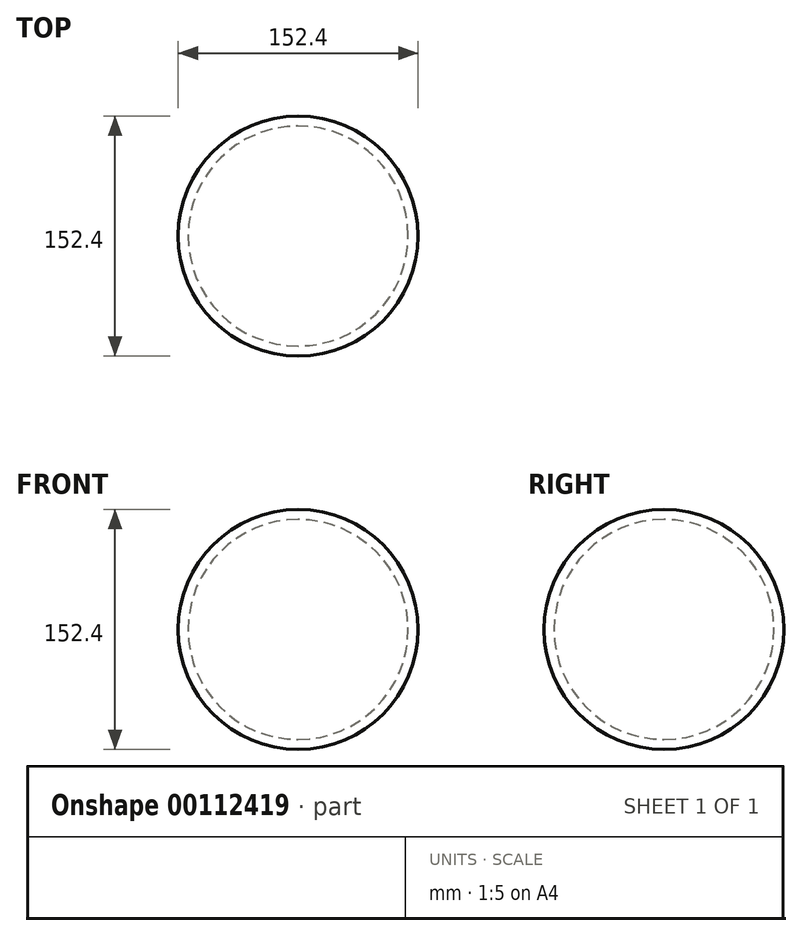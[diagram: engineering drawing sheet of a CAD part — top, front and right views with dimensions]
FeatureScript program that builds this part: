
annotation { "Feature Type Name" : "Feature", "Feature Type Description" : "" }
export const myFeature = defineFeature(function(context is Context, id is Id, definition is map)
    precondition{}
    {
        {
            var Q0;
            Q0=qCreatedBy(makeId("Front.planeOp"),FACE);
            var sketch = newSketch(context, id + "F0", { "sketchPlane" : qUnion([Q0])});
            skCircle(sketch, "E0", {"center": v(0, 0) * mm, "radius": 76.2 * mm});
            skCircle(sketch, "E1", {"center": v(0, 0) * mm, "radius": 69.89 * mm});
            skLineSegment(sketch, "E2", {"start": v(0, 76.2) * mm, "end": v(0, -76.2) * mm});
            skSolve(sketch);
        }
        {
            var Q0;
            {var subQ0=sQuery(id+"F0.wireOp",EDGE,"E2");var subQ1=sQuery(id+"F0.wireOp",EDGE,"E0");var subQ2=makeQuery(id+"F0.imprint","INTERSECT",VERTEX,{"disambiguationData":[OD(0.0)],"derivedFrom":[subQ1,subQ0]});Q0=makeQuery(id+"F0.imprint","IMPRINT",FACE,{"disambiguationData":[TD([[makeQuery(id+"F0.imprint","IMPRINT",EDGE,{"disambiguationData":[TD([[subQ2,-1.0]])],"derivedFrom":subQ1}),1.0]])]});}
            var Q1;
            Q1=sQuery(id+"F0.wireOp",EDGE,"E2");
            revolve(context, id + "F1", {"entities" : qUnion([Q0]), "axis" : qUnion([Q1]), "revolveType" : RevolveType.FULL});
        }
    });
